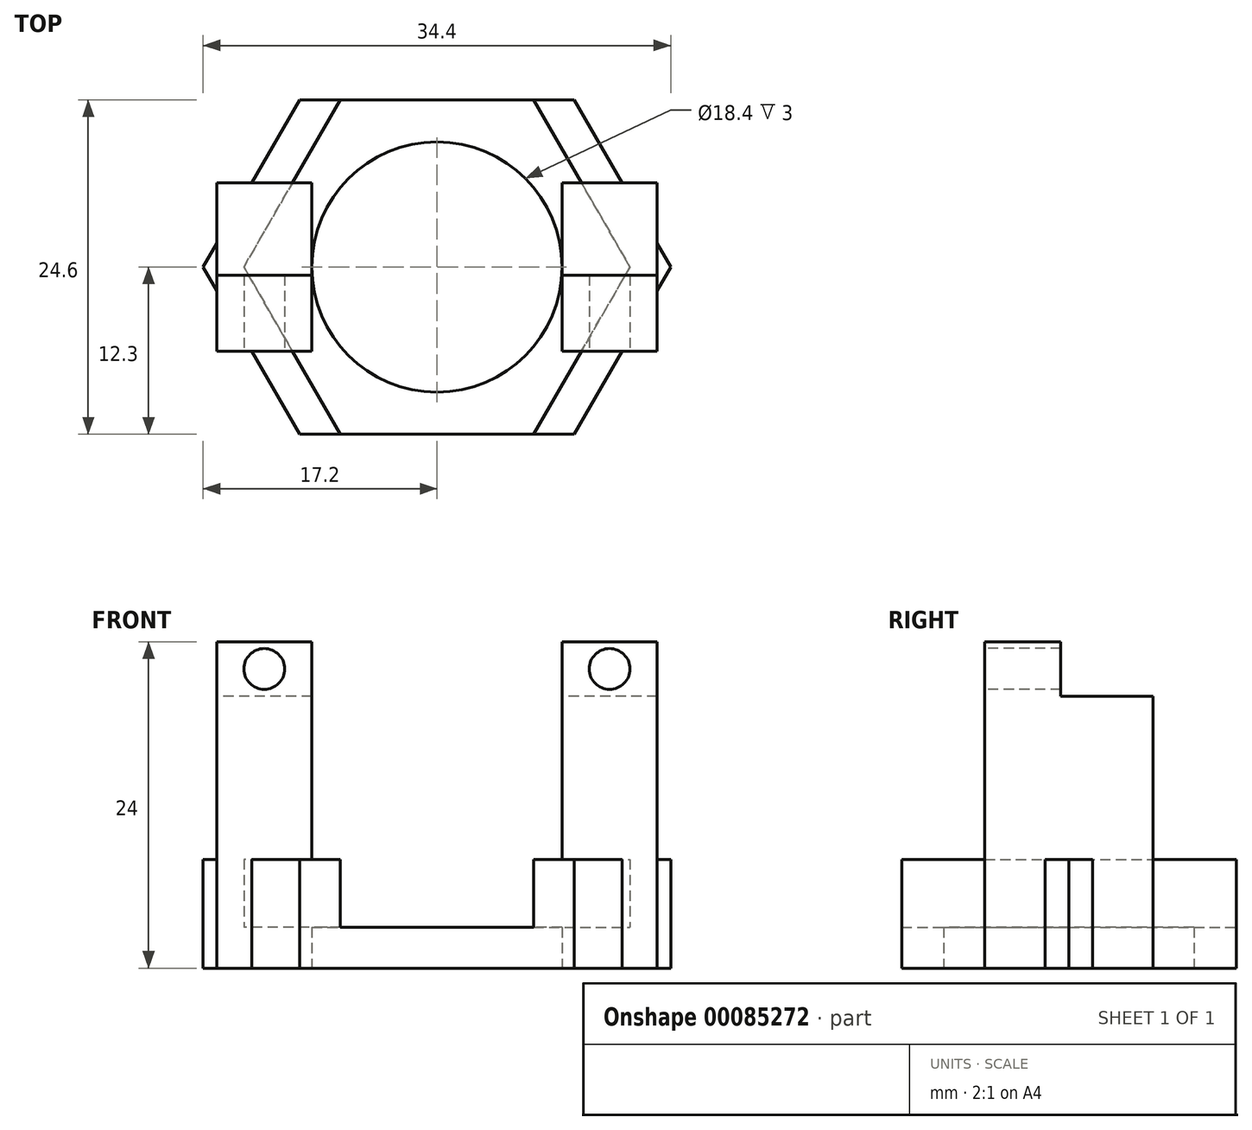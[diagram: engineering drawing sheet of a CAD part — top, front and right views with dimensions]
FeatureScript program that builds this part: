
annotation { "Feature Type Name" : "Feature", "Feature Type Description" : "" }
export const myFeature = defineFeature(function(context is Context, id is Id, definition is map)
    precondition{}
    {
        {
            var Q0;
            Q0=qCreatedBy(makeId("Top.planeOp"),FACE);
            var sketch = newSketch(context, id + "F0", { "sketchPlane" : qUnion([Q0])});
            skCircle(sketch, "E0.cCircle", {"center": v(0, 0) * mm, "radius": 12.3 * mm, "construction": true});
            skLineSegment(sketch, "E0.0", {"start": v(-14.2, 0) * mm, "end": v(-7.1, 12.3) * mm});
            skLineSegment(sketch, "E0.1", {"start": v(-7.1, 12.3) * mm, "end": v(7.1, 12.3) * mm});
            skLineSegment(sketch, "E0.2", {"start": v(7.1, 12.3) * mm, "end": v(14.2, 0) * mm});
            skLineSegment(sketch, "E0.3", {"start": v(14.2, 0) * mm, "end": v(7.1, -12.3) * mm});
            skLineSegment(sketch, "E0.4", {"start": v(7.1, -12.3) * mm, "end": v(-7.1, -12.3) * mm});
            skLineSegment(sketch, "E0.5", {"start": v(-7.1, -12.3) * mm, "end": v(-14.2, 0) * mm});
            skPoint(sketch, "E0.0.midPoint", {"position": v(-10.65, 6.15) * mm});
            skCircle(sketch, "E1", {"center": v(0, 0) * mm, "radius": 9.2 * mm});
            skLineSegment(sketch, "E2", {"start": v(-10.1, 12.3) * mm, "end": v(-17.2, 0) * mm});
            skLineSegment(sketch, "E3", {"start": v(-17.2, 0) * mm, "end": v(-10.1, -12.3) * mm});
            skLineSegment(sketch, "E4", {"start": v(10.1, 12.3) * mm, "end": v(17.2, 0) * mm});
            skLineSegment(sketch, "E5", {"start": v(17.2, 0) * mm, "end": v(10.1, -12.3) * mm});
            skLineSegment(sketch, "E6", {"start": v(10.1, -12.3) * mm, "end": v(7.1, -12.3) * mm});
            skLineSegment(sketch, "E7", {"start": v(-7.1, -12.3) * mm, "end": v(-10.1, -12.3) * mm});
            skLineSegment(sketch, "E8", {"start": v(-10.1, 12.3) * mm, "end": v(-7.1, 12.3) * mm});
            skLineSegment(sketch, "E9", {"start": v(7.1, 12.3) * mm, "end": v(10.1, 12.3) * mm});
            skSolve(sketch);
        }
        {
            var Q0;
            Q0=makeQuery(id+"F0.imprint","IMPRINT",FACE,{"disambiguationData":[TD([[makeQuery(id+"F0.imprint","IMPRINT",EDGE,{"derivedFrom":sQuery(id+"F0.wireOp",EDGE,"E0.0")}),1.0]])]});
            var Q1;
            Q1=makeQuery(id+"F0.imprint","IMPRINT",FACE,{"disambiguationData":[TD([[makeQuery(id+"F0.imprint","IMPRINT",EDGE,{"derivedFrom":sQuery(id+"F0.wireOp",EDGE,"E0.0")}),-1.0]])]});
            var Q2;
            Q2=makeQuery(id+"F0.imprint","IMPRINT",FACE,{"disambiguationData":[TD([[makeQuery(id+"F0.imprint","IMPRINT",EDGE,{"derivedFrom":sQuery(id+"F0.wireOp",EDGE,"E0.2")}),1.0]])]});
            extrude(context, id + "F1", {"entities" : qUnion([Q0, Q1, Q2]), "depth" : 3 * mm});
        }
        {
            var Q0;
            Q0=makeQuery(id+"F0.imprint","IMPRINT",FACE,{"disambiguationData":[TD([[makeQuery(id+"F0.imprint","IMPRINT",EDGE,{"derivedFrom":sQuery(id+"F0.wireOp",EDGE,"E0.0")}),1.0]])]});
            var Q1;
            Q1=makeQuery(id+"F0.imprint","IMPRINT",FACE,{"disambiguationData":[TD([[makeQuery(id+"F0.imprint","IMPRINT",EDGE,{"derivedFrom":sQuery(id+"F0.wireOp",EDGE,"E0.2")}),1.0]])]});
            var Q2;
            Q2=makeQuery(id+"F1.opExtrude","CAP_FACE",FACE,{"disambiguationData":[OSD([sQuery(id+"F0.wireOp",EDGE,"E0.1"),sQuery(id+"F0.wireOp",EDGE,"E0.4"),sQuery(id+"F0.wireOp",EDGE,"E1"),sQuery(id+"F0.wireOp",EDGE,"E2"),sQuery(id+"F0.wireOp",EDGE,"E3"),sQuery(id+"F0.wireOp",EDGE,"E4"),sQuery(id+"F0.wireOp",EDGE,"E5"),sQuery(id+"F0.wireOp",EDGE,"E6"),sQuery(id+"F0.wireOp",EDGE,"E7"),sQuery(id+"F0.wireOp",EDGE,"E8"),sQuery(id+"F0.wireOp",EDGE,"E9")])],"isStart":false});
            extrude(context, id + "F2", {"entities" : qUnion([Q0, Q1]), "operationType" : NewBodyOperationType.ADD, "depth" : (3 + 5) * mm});
        }
        {
            var Q0;
            Q0=makeQuery(id+"F2.opExtrude","CAP_FACE",FACE,{"disambiguationData":[OSD([sQuery(id+"F0.wireOp",EDGE,"E0.0"),sQuery(id+"F0.wireOp",EDGE,"E0.5"),sQuery(id+"F0.wireOp",EDGE,"E2"),sQuery(id+"F0.wireOp",EDGE,"E3"),sQuery(id+"F0.wireOp",EDGE,"E7"),sQuery(id+"F0.wireOp",EDGE,"E8")])],"isStart":false});
            var sketch = newSketch(context, id + "F3", { "sketchPlane" : qUnion([Q0])});
            skLineSegment(sketch, "E10", {"start": v(-9.2, 10.2) * mm, "end": v(9.2, 10.2) * mm, "construction": true});
            skLineSegment(sketch, "E11", {"start": v(9.2, 10.2) * mm, "end": v(9.2, 6.2) * mm, "construction": true});
            skLineSegment(sketch, "E12", {"start": v(9.2, 6.2) * mm, "end": v(16.2, 6.2) * mm});
            skLineSegment(sketch, "E13", {"start": v(-9.2, 10.2) * mm, "end": v(-9.2, 6.2) * mm, "construction": true});
            skLineSegment(sketch, "E14", {"start": v(-9.2, 6.2) * mm, "end": v(-16.2, 6.2) * mm});
            skPoint(sketch, "E15", {"position": v(0, 10.2) * mm});
            skLineSegment(sketch, "E16", {"start": v(-16.2, 6.2) * mm, "end": v(-16.2, -6.2) * mm});
            skLineSegment(sketch, "E17", {"start": v(-9.2, -6.2) * mm, "end": v(-9.2, 6.2) * mm});
            skLineSegment(sketch, "E18.MirrorCS", {"start": v(-9.2, -6.2) * mm, "end": v(-16.2, -6.2) * mm});
            skPoint(sketch, "E19.0", {"position": v(17.2, 0) * mm});
            skPoint(sketch, "E19.1", {"position": v(14.2, 0) * mm});
            skLineSegment(sketch, "E20", {"start": v(14.2, 0) * mm, "end": v(17.2, 0) * mm, "construction": true});
            skLineSegment(sketch, "E21.MirrorCS", {"start": v(9.2, -6.2) * mm, "end": v(16.2, -6.2) * mm});
            skLineSegment(sketch, "E22", {"start": v(16.2, 6.2) * mm, "end": v(16.2, -6.2) * mm});
            skLineSegment(sketch, "E23", {"start": v(9.2, 6.2) * mm, "end": v(9.2, -6.2) * mm});
            skPoint(sketch, "E24.0", {"position": v(-17.2, 0) * mm});
            skPoint(sketch, "E24.1", {"position": v(-14.2, 0) * mm});
            skLineSegment(sketch, "E25", {"start": v(-14.2, 0) * mm, "end": v(-17.2, 0) * mm, "construction": true});
            skSolve(sketch);
        }
        {
            var Q0;
            {var subQ6=sQuery(id+"F3.wireOp",EDGE,"E16");Q0=makeQuery(id+"F3.imprint","IMPRINT",FACE,{"disambiguationData":[TD([[makeQuery(id+"F3.imprint","IMPRINT",EDGE,{"derivedFrom":subQ6}),1.0]])]});}
            var Q1;
            {var subQ1=makeQuery(id+"F2.opExtrude","CAP_EDGE",EDGE,{"disambiguationData":[OSD([sQuery(id+"F0.wireOp",EDGE,"E0.0")])],"isStart":false});var subQ3=sQuery(id+"F3.wireOp",EDGE,"E14");var subQ4=makeQuery(id+"F3.imprint","INTERSECT",VERTEX,{"derivedFrom":[subQ1,subQ3]});Q1=makeQuery(id+"F3.imprint","IMPRINT",FACE,{"disambiguationData":[TD([[makeQuery(id+"F3.imprint","IMPRINT",EDGE,{"disambiguationData":[TD([[subQ4,-1.0]])],"derivedFrom":subQ3}),1.0]])]});}
            var Q2;
            {var subQ6=sQuery(id+"F3.wireOp",EDGE,"E17");Q2=makeQuery(id+"F3.imprint","IMPRINT",FACE,{"disambiguationData":[TD([[makeQuery(id+"F3.imprint","IMPRINT",EDGE,{"derivedFrom":subQ6}),1.0]])]});}
            var Q3;
            Q3=makeQuery(id+"F3.imprint","IMPRINT",FACE,{"disambiguationData":[TD([[makeQuery(id+"F3.imprint","IMPRINT",EDGE,{"derivedFrom":sQuery(id+"F3.wireOp",EDGE,"E12")}),-1.0]])]});
            extrude(context, id + "F4", {"entities" : qUnion([Q0, Q1, Q2, Q3]), "operationType" : NewBodyOperationType.ADD, "depth" : ((20 - 5 - 3) + 4) * mm});
        }
        {
            var Q0;
            {var subQ0=sQuery(id+"F0.wireOp",EDGE,"E2");var subQ2=sQuery(id+"F3.wireOp",EDGE,"E18.MirrorCS");var subQ3=sQuery(id+"F3.wireOp",EDGE,"E14");var subQ4=sQuery(id+"F3.wireOp",EDGE,"E16");Q0=makeQuery(id+"F4.boolean.opBoolean","SPLIT",FACE,{"disambiguationData":[TD([makeQuery(id+"F1.opExtrude","SWEPT_FACE",FACE,{"disambiguationData":[OSD([subQ0])]})])],"derivedFrom":makeQuery(id+"F4.opExtrude","CAP_FACE",FACE,{"disambiguationData":[OSD([subQ3,subQ4,sQuery(id+"F3.wireOp",EDGE,"E17"),subQ2])],"isStart":true})});}
            var Q1;
            {var subQ0=sQuery(id+"F0.wireOp",EDGE,"E4");var subQ1=sQuery(id+"F3.wireOp",EDGE,"E12");var subQ3=sQuery(id+"F3.wireOp",EDGE,"E21.MirrorCS");var subQ4=sQuery(id+"F3.wireOp",EDGE,"E22");Q1=makeQuery(id+"F4.boolean.opBoolean","SPLIT",FACE,{"disambiguationData":[TD([makeQuery(id+"F1.opExtrude","SWEPT_FACE",FACE,{"disambiguationData":[OSD([subQ0])]})])],"derivedFrom":makeQuery(id+"F4.opExtrude","CAP_FACE",FACE,{"disambiguationData":[OSD([subQ1,subQ3,subQ4,sQuery(id+"F3.wireOp",EDGE,"E23")])],"isStart":true})});}
            var Q2;
            {var subQ0=sQuery(id+"F3.wireOp",EDGE,"E21.MirrorCS");var subQ1=sQuery(id+"F0.wireOp",EDGE,"E5");var subQ2=sQuery(id+"F3.wireOp",EDGE,"E22");Q2=makeQuery(id+"F4.boolean.opBoolean","SPLIT",FACE,{"disambiguationData":[TD([makeQuery(id+"F1.opExtrude","SWEPT_FACE",FACE,{"disambiguationData":[OSD([subQ1])]})])],"derivedFrom":makeQuery(id+"F4.opExtrude","CAP_FACE",FACE,{"disambiguationData":[OSD([sQuery(id+"F3.wireOp",EDGE,"E12"),subQ0,subQ2,sQuery(id+"F3.wireOp",EDGE,"E23")])],"isStart":true})});}
            var Q3;
            {var subQ0=sQuery(id+"F3.wireOp",EDGE,"E16");var subQ1=sQuery(id+"F0.wireOp",EDGE,"E3");var subQ2=sQuery(id+"F3.wireOp",EDGE,"E18.MirrorCS");Q3=makeQuery(id+"F4.boolean.opBoolean","SPLIT",FACE,{"disambiguationData":[TD([makeQuery(id+"F1.opExtrude","SWEPT_FACE",FACE,{"disambiguationData":[OSD([subQ1])]})])],"derivedFrom":makeQuery(id+"F4.opExtrude","CAP_FACE",FACE,{"disambiguationData":[OSD([sQuery(id+"F3.wireOp",EDGE,"E14"),subQ0,sQuery(id+"F3.wireOp",EDGE,"E17"),subQ2])],"isStart":true})});}
            var Q4;
            Q4=makeQuery(id+"F1.opExtrude","CAP_FACE",FACE,{"disambiguationData":[OSD([sQuery(id+"F0.wireOp",EDGE,"E0.1"),sQuery(id+"F0.wireOp",EDGE,"E0.4"),sQuery(id+"F0.wireOp",EDGE,"E1"),sQuery(id+"F0.wireOp",EDGE,"E2"),sQuery(id+"F0.wireOp",EDGE,"E3"),sQuery(id+"F0.wireOp",EDGE,"E4"),sQuery(id+"F0.wireOp",EDGE,"E5"),sQuery(id+"F0.wireOp",EDGE,"E6"),sQuery(id+"F0.wireOp",EDGE,"E7"),sQuery(id+"F0.wireOp",EDGE,"E8"),sQuery(id+"F0.wireOp",EDGE,"E9")])],"isStart":true});
            extrude(context, id + "F5", {"entities" : qUnion([Q0, Q1, Q2, Q3]), "operationType" : NewBodyOperationType.ADD, "endBound" : BoundingType.UP_TO_SURFACE, "endBoundEntityFace" : qUnion([Q4]), "depth" : 25 * mm});
        }
        {
            var Q0;
            {var subQ0=sQuery(id+"F3.wireOp",EDGE,"E18.MirrorCS");Q0=makeQuery(id+"F5.boolean.opBoolean","MERGE",FACE,{"derivedFrom":[makeQuery(id+"F4.opExtrude","SWEPT_FACE",FACE,{"disambiguationData":[OSD([subQ0])]}),makeQuery(id+"F5.opExtrude","SWEPT_FACE",FACE,{"disambiguationData":[OSD([subQ0])]})]});}
            var sketch = newSketch(context, id + "F6", { "sketchPlane" : qUnion([Q0])});
            skLineSegment(sketch, "E26.1", {"start": v(-9.2, 24) * mm, "end": v(-16.2, 24) * mm});
            skLineSegment(sketch, "E26.2", {"start": v(-9.2, 24) * mm, "end": v(-9.2, 8) * mm});
            skLineSegment(sketch, "E26.3", {"start": v(9.2, 24) * mm, "end": v(9.2, 8) * mm});
            skLineSegment(sketch, "E26.4", {"start": v(9.2, 24) * mm, "end": v(16.2, 24) * mm});
            skLineSegment(sketch, "E26.5", {"start": v(16.2, 24) * mm, "end": v(16.2, 0) * mm});
            skLineSegment(sketch, "E27", {"start": v(-16.2, 20) * mm, "end": v(-9.2, 20) * mm});
            skLineSegment(sketch, "E28", {"start": v(9.2, 20) * mm, "end": v(16.2, 20) * mm});
            skLineSegment(sketch, "E29", {"start": v(-16.2, 24) * mm, "end": v(-16.2, 20) * mm});
            skLineSegment(sketch, "E30", {"start": v(9.2, 24) * mm, "end": v(9.2, 20) * mm, "construction": true});
            skCircle(sketch, "E31", {"center": v(-12.7, 22) * mm, "radius": 1.5 * mm});
            skPoint(sketch, "E31.centerSnap0", {"position": v(-12.7, 20) * mm});
            skPoint(sketch, "E31.centerSnap1", {"position": v(-16.2, 22) * mm});
            skCircle(sketch, "E32", {"center": v(12.7, 22) * mm, "radius": 1.5 * mm});
            skPoint(sketch, "E32.centerSnap0", {"position": v(9.2, 22) * mm});
            skPoint(sketch, "E32.centerSnap1", {"position": v(12.7, 20) * mm});
            skSolve(sketch);
        }
        {
            var Q0;
            Q0=makeQuery(id+"F6.imprint","IMPRINT",FACE,{"disambiguationData":[TD([[makeQuery(id+"F6.imprint","IMPRINT",EDGE,{"derivedFrom":sQuery(id+"F6.wireOp",EDGE,"E31")}),1.0]])]});
            var Q1;
            Q1=makeQuery(id+"F6.imprint","IMPRINT",FACE,{"disambiguationData":[TD([[makeQuery(id+"F6.imprint","IMPRINT",EDGE,{"derivedFrom":sQuery(id+"F6.wireOp",EDGE,"E32")}),1.0]])]});
            extrude(context, id + "F7", {"entities" : qUnion([Q0, Q1]), "operationType" : NewBodyOperationType.REMOVE, "endBound" : BoundingType.THROUGH_ALL, "oppositeDirection" : true, "depth" : 25 * mm});
        }
        {
            var Q0;
            {var subQ2=sQuery(id+"F6.wireOp",EDGE,"E26.1");Q0=makeQuery(id+"F6.imprint","IMPRINT",FACE,{"disambiguationData":[TD([[makeQuery(id+"F6.imprint","IMPRINT",EDGE,{"derivedFrom":subQ2}),1.0]])]});}
            var Q1;
            {var subQ1=sQuery(id+"F6.wireOp",EDGE,"E26.4");Q1=makeQuery(id+"F6.imprint","IMPRINT",FACE,{"disambiguationData":[TD([[makeQuery(id+"F6.imprint","IMPRINT",EDGE,{"derivedFrom":subQ1}),-1.0]])]});}
            var Q2;
            {var subQ0=sQuery(id+"F3.wireOp",EDGE,"E14");Q2=makeQuery(id+"F5.boolean.opBoolean","MERGE",FACE,{"derivedFrom":[makeQuery(id+"F4.opExtrude","SWEPT_FACE",FACE,{"disambiguationData":[OSD([subQ0])]}),makeQuery(id+"F5.opExtrude","SWEPT_FACE",FACE,{"disambiguationData":[OSD([subQ0])]})]});}
            extrude(context, id + "F8", {"entities" : qUnion([Q0, Q1]), "operationType" : NewBodyOperationType.REMOVE, "endBound" : BoundingType.UP_TO_SURFACE, "oppositeDirection" : true, "endBoundEntityFace" : qUnion([Q2]), "depth" : 25 * mm, "hasSecondDirection" : true, "secondDirectionOppositeDirection" : true, "secondDirectionDepth" : 5.6 * mm});
        }
    });
